# Revit family: NLRS_50_ME_UN_AV_douchedrain-Joulia-twinline_J6  DR-10P-830-R_ARCH
name_source: partatom
category: Mechanical Equipment
revit_build: Autodesk Revit 2017 (Build: 20181011_1645(x64)
units: mm (PartAtom-declared; Revit-internal decimal feet)

## family parameters
Always vertical = Yes
Cut with Voids When Loaded = Yes
Part Type = Normal
Room Calculation Point = No
Round Connector Dimension = Use Diameter
Shared = No
Work Plane-Based = No

## types (1)
- twinline_J6 DR-10P-830-R
    Description = douchegoot met 3-pijps warmtewisselaar voor verzonken montage
    IfcDescription = douchegoot met 3-pijps warmtewisselaar voor verzonken montage
    IfcExportAs = IfcHeatExchangerType
    IfcExportType = USERDEFINED
    Manufacturer = Joulia
    Model = Joulia J3 / DR-3P-630-R
    NLRS_C_code_STABU = 50
    NLRS_C_code_SfB_tabel1 = 52
    NLRS_C_diepte-vloergat = -118.5 mm  [stored -0.38878 ft]
    NLRS_C_leverancier_bedrijfsnaam = Technea
    NLRS_C_niveau ontwikkeling = LOD 400
    NLRS_P_c01_aansluitmethode = Lijmmof
    NLRS_P_c02_aansluitmethode = koutwater aansluiting
    NLRS_P_c03_aansluitmethode = verwarmde wateraansluiting naar thermostaatkraan
    RSen_C_code_manufacturer_gln = -
    RSen_C_content_version = 1.0
    RSen_C_material_colour = RVS
    URL = https://joulia.com

note: [stored X ft] marks values corroborated as IEEE doubles in the binary element streams (Revit-internal decimal feet)

## geometry (parser evidence)
native form markers: Sweep x56
no freeform markers — native parametric forms only
